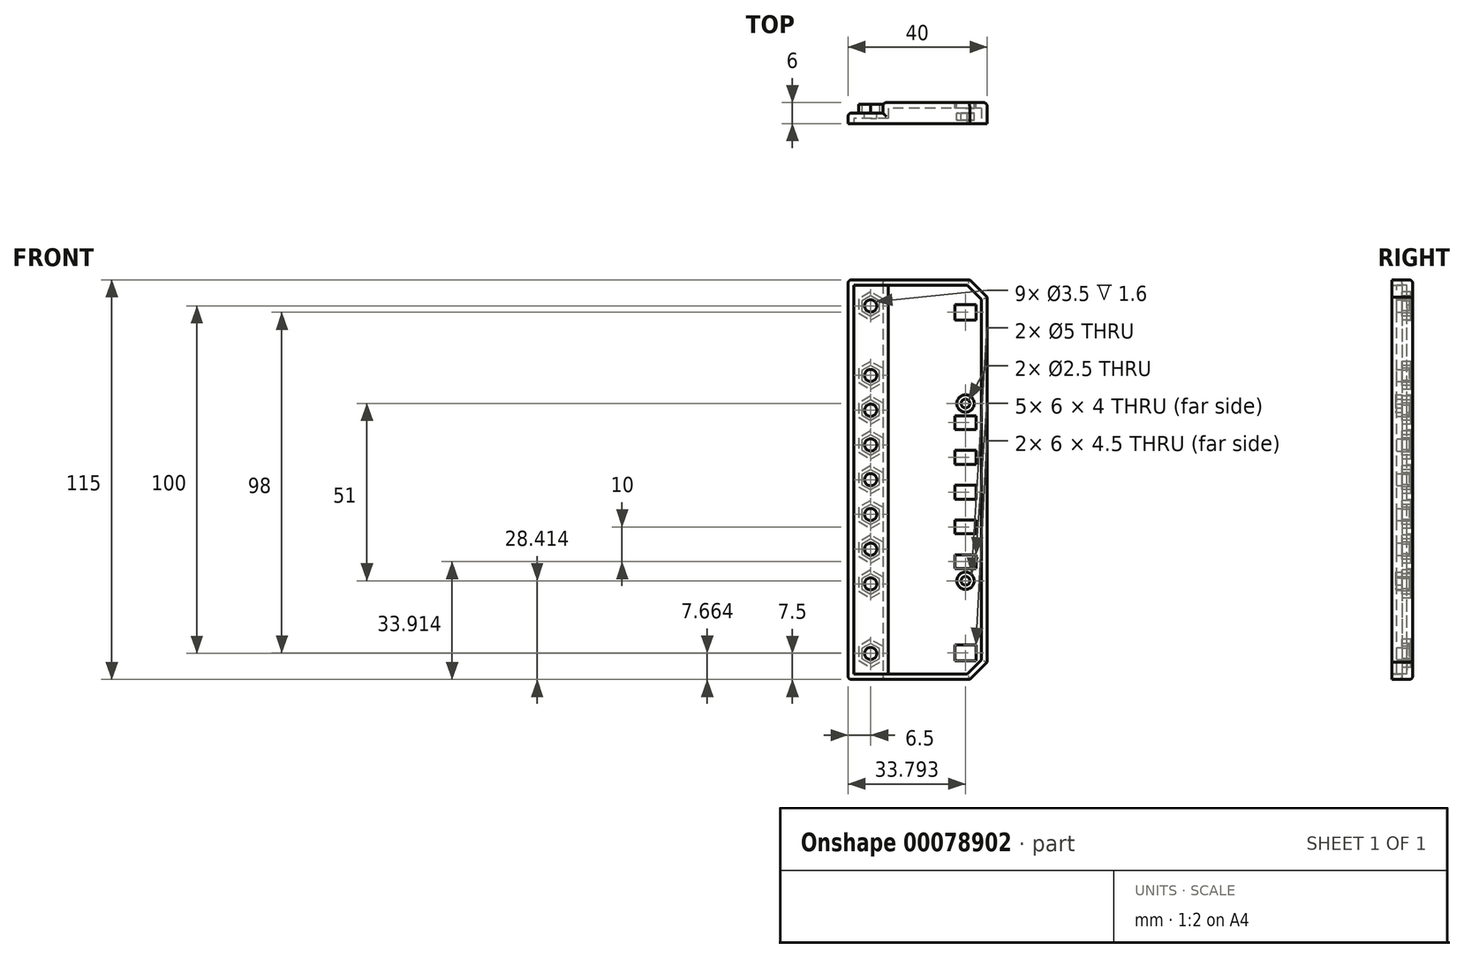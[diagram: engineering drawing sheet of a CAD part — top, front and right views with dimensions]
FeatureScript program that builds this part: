
annotation { "Feature Type Name" : "Feature", "Feature Type Description" : "" }
export const myFeature = defineFeature(function(context is Context, id is Id, definition is map)
    precondition{}
    {
        {
            var Q0;
            Q0=qCreatedBy(makeId("Top.planeOp"),FACE);
            var sketch = newSketch(context, id + "F0", { "sketchPlane" : qUnion([Q0])});
            skLineSegment(sketch, "E0", {"start": v(-20, 3) * mm, "end": v(-20, 0) * mm});
            skLineSegment(sketch, "E1", {"start": v(-20, 0) * mm, "end": v(20, 0) * mm});
            skLineSegment(sketch, "E2", {"start": v(20, 0) * mm, "end": v(20, 6) * mm});
            skLineSegment(sketch, "E3", {"start": v(20, 6) * mm, "end": v(-10, 6) * mm});
            skLineSegment(sketch, "E4", {"start": v(-10, 6) * mm, "end": v(-10, 3) * mm});
            skLineSegment(sketch, "E5", {"start": v(-10, 3) * mm, "end": v(-20, 3) * mm});
            skSolve(sketch);
        }
        {
            var Q0;
            Q0 = qSketchRegion(id + "F0", true);
            extrude(context, id + "F1", {"entities" : qUnion([Q0]), "depth" : 115 * mm});
        }
        {
            var Q0;
            Q0=makeQuery(id+"F1.opExtrude","CAP_EDGE",EDGE,{"disambiguationData":[OSD([sQuery(id+"F0.wireOp",EDGE,"E2")])],"isStart":false});
            var Q1;
            Q1=makeQuery(id+"F1.opExtrude","CAP_EDGE",EDGE,{"disambiguationData":[OSD([sQuery(id+"F0.wireOp",EDGE,"E2")])],"isStart":true});
            chamfer(context, id + "F2", {"entities" : qUnion([Q0, Q1]), "width" : 5 * mm, "tangentPropagation" : true});
        }
        {
            var Q0;
            Q0=makeQuery(id+"F1.opExtrude","CAP_EDGE",EDGE,{"disambiguationData":[OSD([sQuery(id+"F0.wireOp",EDGE,"E0")])],"isStart":true});
            var Q1;
            Q1=makeQuery(id+"F1.opExtrude","CAP_EDGE",EDGE,{"disambiguationData":[OSD([sQuery(id+"F0.wireOp",EDGE,"E4")])],"isStart":true});
            var Q2;
            Q2=makeQuery(id+"F1.opExtrude","CAP_EDGE",EDGE,{"disambiguationData":[OSD([sQuery(id+"F0.wireOp",EDGE,"E4")])],"isStart":false});
            var Q3;
            Q3=makeQuery(id+"F1.opExtrude","CAP_EDGE",EDGE,{"disambiguationData":[OSD([sQuery(id+"F0.wireOp",EDGE,"E0")])],"isStart":false});
            var Q4;
            Q4=makeQuery(id+"F1.opExtrude","SWEPT_EDGE",EDGE,{"disambiguationData":[OSD([sQuery(id+"F0.wireOp",EDGE,"E3"),sQuery(id+"F0.wireOp",EDGE,"E4")])]});
            var Q5;
            Q5=makeQuery(id+"F1.opExtrude","SWEPT_EDGE",EDGE,{"disambiguationData":[OSD([sQuery(id+"F0.wireOp",EDGE,"E0"),sQuery(id+"F0.wireOp",EDGE,"E5")])]});
            var Q6;
            Q6=makeQuery(id+"F1.opExtrude","CAP_EDGE",EDGE,{"disambiguationData":[OSD([sQuery(id+"F0.wireOp",EDGE,"E5")])],"isStart":true});
            var Q7;
            Q7=makeQuery(id+"F1.opExtrude","CAP_EDGE",EDGE,{"disambiguationData":[OSD([sQuery(id+"F0.wireOp",EDGE,"E5")])],"isStart":false});
            var Q8;
            Q8=makeQuery(id+"F1.opExtrude","CAP_EDGE",EDGE,{"disambiguationData":[OSD([sQuery(id+"F0.wireOp",EDGE,"E3")])],"isStart":false});
            var Q9;
            Q9=makeQuery(id+"F1.opExtrude","SWEPT_EDGE",EDGE,{"disambiguationData":[OSD([sQuery(id+"F0.wireOp",EDGE,"E2"),sQuery(id+"F0.wireOp",EDGE,"E3")])]});
            var Q10;
            Q10=makeQuery(id+"F1.opExtrude","CAP_EDGE",EDGE,{"disambiguationData":[OSD([sQuery(id+"F0.wireOp",EDGE,"E3")])],"isStart":true});
            var Q11;
            Q11=makeQuery(id+"F2.opChamfer","BLEND_EDGE",EDGE,{"blendedFrom":[makeQuery(id+"F1.opExtrude","CAP_EDGE",EDGE,{"disambiguationData":[OSD([sQuery(id+"F0.wireOp",EDGE,"E2")])],"isStart":false}),makeQuery(id+"F1.opExtrude","SWEPT_FACE",FACE,{"disambiguationData":[OSD([sQuery(id+"F0.wireOp",EDGE,"E3")])]})],"blendedInto":[makeQuery(id+"F1.opExtrude","SWEPT_FACE",FACE,{"disambiguationData":[OSD([sQuery(id+"F0.wireOp",EDGE,"E3")])]})]});
            var Q12;
            Q12=makeQuery(id+"F2.opChamfer","BLEND_EDGE",EDGE,{"blendedFrom":[makeQuery(id+"F1.opExtrude","CAP_EDGE",EDGE,{"disambiguationData":[OSD([sQuery(id+"F0.wireOp",EDGE,"E2")])],"isStart":true}),makeQuery(id+"F1.opExtrude","SWEPT_FACE",FACE,{"disambiguationData":[OSD([sQuery(id+"F0.wireOp",EDGE,"E3")])]})],"blendedInto":[makeQuery(id+"F1.opExtrude","SWEPT_FACE",FACE,{"disambiguationData":[OSD([sQuery(id+"F0.wireOp",EDGE,"E3")])]})]});
            fillet(context, id + "F3", {"entities" : qUnion([Q0, Q1, Q2, Q3, Q4, Q5, Q6, Q7, Q8, Q9, Q10, Q11, Q12]), "radius" : 1 * mm, "tangentPropagation" : true, "allowEdgeOverflow" : false});
        }
        {
            var Q0;
            Q0=makeQuery(id+"F1.opExtrude","SWEPT_FACE",FACE,{"disambiguationData":[OSD([sQuery(id+"F0.wireOp",EDGE,"E1")])]});
            shell(context, id + "F4", {"entities" : qUnion([Q0]), "thickness" : 1.6 * mm});
        }
        {
            var Q0;
            Q0=makeQuery(id+"F1.opExtrude","SWEPT_FACE",FACE,{"disambiguationData":[OSD([sQuery(id+"F0.wireOp",EDGE,"E3")])]});
            var sketch = newSketch(context, id + "F5", { "sketchPlane" : qUnion([Q0])});
            skLineSegment(sketch, "E6.0", {"start": v(-20, 5) * mm, "end": v(-20, 110) * mm});
            skLineSegment(sketch, "E7.bottom", {"start": v(-10.8, 75.91) * mm, "end": v(-16.8, 75.91) * mm});
            skLineSegment(sketch, "E7.top", {"start": v(-10.8, 71.91) * mm, "end": v(-16.8, 71.91) * mm});
            skLineSegment(sketch, "E7.left", {"start": v(-10.8, 75.91) * mm, "end": v(-10.8, 71.91) * mm});
            skLineSegment(sketch, "E7.right", {"start": v(-16.8, 75.91) * mm, "end": v(-16.8, 71.91) * mm});
            skLineSegment(sketch, "E8.0.1.0", {"start": v(-10.8, 65.91) * mm, "end": v(-16.8, 65.91) * mm});
            skLineSegment(sketch, "E8.0.1.1", {"start": v(-10.8, 61.91) * mm, "end": v(-16.8, 61.91) * mm});
            skLineSegment(sketch, "E8.0.1.2", {"start": v(-10.8, 65.91) * mm, "end": v(-10.8, 61.91) * mm});
            skLineSegment(sketch, "E8.0.1.3", {"start": v(-16.8, 65.91) * mm, "end": v(-16.8, 61.91) * mm});
            skLineSegment(sketch, "E8.0.2.0", {"start": v(-10.8, 55.91) * mm, "end": v(-16.8, 55.91) * mm});
            skLineSegment(sketch, "E8.0.2.1", {"start": v(-10.8, 51.91) * mm, "end": v(-16.8, 51.91) * mm});
            skLineSegment(sketch, "E8.0.2.2", {"start": v(-10.8, 55.91) * mm, "end": v(-10.8, 51.91) * mm});
            skLineSegment(sketch, "E8.0.2.3", {"start": v(-16.8, 55.91) * mm, "end": v(-16.8, 51.91) * mm});
            skLineSegment(sketch, "E8.0.3.0", {"start": v(-10.8, 45.91) * mm, "end": v(-16.8, 45.91) * mm});
            skLineSegment(sketch, "E8.0.3.1", {"start": v(-10.8, 41.91) * mm, "end": v(-16.8, 41.91) * mm});
            skLineSegment(sketch, "E8.0.3.2", {"start": v(-10.8, 45.91) * mm, "end": v(-10.8, 41.91) * mm});
            skLineSegment(sketch, "E8.0.3.3", {"start": v(-16.8, 45.91) * mm, "end": v(-16.8, 41.91) * mm});
            skLineSegment(sketch, "E8.0.4.0", {"start": v(-10.8, 35.91) * mm, "end": v(-16.8, 35.91) * mm});
            skLineSegment(sketch, "E8.0.4.1", {"start": v(-10.8, 31.91) * mm, "end": v(-16.8, 31.91) * mm});
            skLineSegment(sketch, "E8.0.4.2", {"start": v(-10.8, 35.91) * mm, "end": v(-10.8, 31.91) * mm});
            skLineSegment(sketch, "E8.0.4.3", {"start": v(-16.8, 35.91) * mm, "end": v(-16.8, 31.91) * mm});
            skLineSegment(sketch, "E8.direction1", {"start": v(-16.8, 71.91) * mm, "end": v(-17, 71.91) * mm, "construction": true});
            skLineSegment(sketch, "E8.direction2", {"start": v(-16.8, 71.91) * mm, "end": v(-16.8, 61.91) * mm, "construction": true});
            skCircle(sketch, "E9", {"center": v(-13.8, 79.41) * mm, "radius": 2.5 * mm});
            skPoint(sketch, "E9.centerSnap0", {"position": v(-13.8, 75.91) * mm});
            skCircle(sketch, "E10", {"center": v(-13.8, 28.41) * mm, "radius": 2.5 * mm});
            skPoint(sketch, "E10.centerSnap0", {"position": v(-13.8, 31.91) * mm});
            skCircle(sketch, "E11", {"center": v(-13.8, 28.41) * mm, "radius": 1.25 * mm});
            skCircle(sketch, "E12", {"center": v(-13.8, 79.41) * mm, "radius": 1.25 * mm});
            skLineSegment(sketch, "E13.bottom", {"start": v(-10.8, 103.41) * mm, "end": v(-16.8, 103.41) * mm});
            skLineSegment(sketch, "E13.top", {"start": v(-10.8, 107.91) * mm, "end": v(-16.8, 107.91) * mm});
            skLineSegment(sketch, "E13.left", {"start": v(-10.8, 103.41) * mm, "end": v(-10.8, 107.91) * mm});
            skLineSegment(sketch, "E13.right", {"start": v(-16.8, 103.41) * mm, "end": v(-16.8, 107.91) * mm});
            skPoint(sketch, "E13.middle", {"position": v(-13.8, 105.66) * mm});
            skLineSegment(sketch, "E14.bottom", {"start": v(-16.8, 5.41) * mm, "end": v(-10.8, 5.41) * mm});
            skLineSegment(sketch, "E14.top", {"start": v(-16.8, 9.91) * mm, "end": v(-10.8, 9.91) * mm});
            skLineSegment(sketch, "E14.left", {"start": v(-16.8, 5.41) * mm, "end": v(-16.8, 9.91) * mm});
            skLineSegment(sketch, "E14.right", {"start": v(-10.8, 5.41) * mm, "end": v(-10.8, 9.91) * mm});
            skPoint(sketch, "E14.middle", {"position": v(-13.8, 7.66) * mm});
            skPoint(sketch, "E14.cornerSnap0", {"position": v(-16.8, 3.2) * mm});
            skSolve(sketch);
        }
        {
            var Q0;
            Q0=makeQuery(id+"F5.imprint","IMPRINT",FACE,{"disambiguationData":[TD([[makeQuery(id+"F5.imprint","IMPRINT",EDGE,{"derivedFrom":sQuery(id+"F5.wireOp",EDGE,"E7.bottom")}),1.0]])]});
            var Q1;
            Q1=makeQuery(id+"F5.imprint","IMPRINT",FACE,{"disambiguationData":[TD([[makeQuery(id+"F5.imprint","IMPRINT",EDGE,{"derivedFrom":sQuery(id+"F5.wireOp",EDGE,"E8.0.1.0")}),1.0]])]});
            var Q2;
            Q2=makeQuery(id+"F5.imprint","IMPRINT",FACE,{"disambiguationData":[TD([[makeQuery(id+"F5.imprint","IMPRINT",EDGE,{"derivedFrom":sQuery(id+"F5.wireOp",EDGE,"E8.0.2.0")}),1.0]])]});
            var Q3;
            Q3=makeQuery(id+"F5.imprint","IMPRINT",FACE,{"disambiguationData":[TD([[makeQuery(id+"F5.imprint","IMPRINT",EDGE,{"derivedFrom":sQuery(id+"F5.wireOp",EDGE,"E8.0.3.0")}),1.0]])]});
            var Q4;
            Q4=makeQuery(id+"F5.imprint","IMPRINT",FACE,{"disambiguationData":[TD([[makeQuery(id+"F5.imprint","IMPRINT",EDGE,{"derivedFrom":sQuery(id+"F5.wireOp",EDGE,"E8.0.4.0")}),1.0]])]});
            var Q5;
            Q5=makeQuery(id+"F5.imprint","IMPRINT",FACE,{"disambiguationData":[TD([[makeQuery(id+"F5.imprint","IMPRINT",EDGE,{"derivedFrom":sQuery(id+"F5.wireOp",EDGE,"E13.bottom")}),-1.0]])]});
            var Q6;
            Q6=makeQuery(id+"F5.imprint","IMPRINT",FACE,{"disambiguationData":[TD([[makeQuery(id+"F5.imprint","IMPRINT",EDGE,{"derivedFrom":sQuery(id+"F5.wireOp",EDGE,"E14.bottom")}),1.0]])]});
            var Q7;
            Q7=makeQuery(id+"F5.imprint","IMPRINT",FACE,{"disambiguationData":[TD([[makeQuery(id+"F5.imprint","IMPRINT",EDGE,{"derivedFrom":sQuery(id+"F5.wireOp",EDGE,"E12")}),1.0]])]});
            var Q8;
            Q8=makeQuery(id+"F5.imprint","IMPRINT",FACE,{"disambiguationData":[TD([[makeQuery(id+"F5.imprint","IMPRINT",EDGE,{"derivedFrom":sQuery(id+"F5.wireOp",EDGE,"E11")}),1.0]])]});
            extrude(context, id + "F6", {"entities" : qUnion([Q0, Q1, Q2, Q3, Q4, Q5, Q6, Q7, Q8]), "operationType" : NewBodyOperationType.REMOVE, "oppositeDirection" : true, "depth" : 100 * mm});
        }
        {
            var Q0;
            Q0=makeQuery(id+"F5.imprint","IMPRINT",FACE,{"disambiguationData":[TD([[makeQuery(id+"F5.imprint","IMPRINT",EDGE,{"derivedFrom":sQuery(id+"F5.wireOp",EDGE,"E9")}),1.0]])]});
            var Q1;
            Q1=makeQuery(id+"F5.imprint","IMPRINT",FACE,{"disambiguationData":[TD([[makeQuery(id+"F5.imprint","IMPRINT",EDGE,{"derivedFrom":sQuery(id+"F5.wireOp",EDGE,"E10")}),1.0]])]});
            extrude(context, id + "F7", {"entities" : qUnion([Q0, Q1]), "operationType" : NewBodyOperationType.ADD, "oppositeDirection" : true, "depth" : 5 * mm});
        }
        {
            var Q0;
            Q0=makeQuery(id+"F1.opExtrude","SWEPT_FACE",FACE,{"disambiguationData":[OSD([sQuery(id+"F0.wireOp",EDGE,"E5")])]});
            var sketch = newSketch(context, id + "F8", { "sketchPlane" : qUnion([Q0])});
            skCircle(sketch, "E15", {"center": v(13.5, 107.5) * mm, "radius": 1.75 * mm});
            skLineSegment(sketch, "E16.0.3", {"start": v(20, 1) * mm, "end": v(20, 114) * mm});
            skCircle(sketch, "E17.0.1.0", {"center": v(13.5, 97.5) * mm, "radius": 1.75 * mm});
            skCircle(sketch, "E17.0.2.0", {"center": v(13.5, 87.5) * mm, "radius": 1.75 * mm});
            skCircle(sketch, "E17.0.3.0", {"center": v(13.5, 77.5) * mm, "radius": 1.75 * mm});
            skCircle(sketch, "E17.0.4.0", {"center": v(13.5, 67.5) * mm, "radius": 1.75 * mm});
            skCircle(sketch, "E17.0.5.0", {"center": v(13.5, 57.5) * mm, "radius": 1.75 * mm});
            skCircle(sketch, "E17.0.6.0", {"center": v(13.5, 47.5) * mm, "radius": 1.75 * mm});
            skCircle(sketch, "E17.0.7.0", {"center": v(13.5, 37.5) * mm, "radius": 1.75 * mm});
            skCircle(sketch, "E17.0.8.0", {"center": v(13.5, 27.5) * mm, "radius": 1.75 * mm});
            skCircle(sketch, "E17.0.9.0", {"center": v(13.5, 17.5) * mm, "radius": 1.75 * mm});
            skCircle(sketch, "E17.0.10.0", {"center": v(13.5, 7.5) * mm, "radius": 1.75 * mm});
            skLineSegment(sketch, "E17.direction1", {"start": v(13.5, 107.5) * mm, "end": v(16.25, 107.5) * mm, "construction": true});
            skLineSegment(sketch, "E17.direction2", {"start": v(13.5, 107.5) * mm, "end": v(13.5, 97.5) * mm, "construction": true});
            skPoint(sketch, "E18", {"position": v(20, 57.5) * mm});
            skCircle(sketch, "E19.cCircle", {"center": v(13.5, 7.5) * mm, "radius": 3.5 * mm, "construction": true});
            skLineSegment(sketch, "E19.0", {"start": v(10, 9.52) * mm, "end": v(13.5, 11.54) * mm});
            skLineSegment(sketch, "E19.1", {"start": v(13.5, 11.54) * mm, "end": v(17, 9.52) * mm});
            skLineSegment(sketch, "E19.2", {"start": v(17, 9.52) * mm, "end": v(17, 5.48) * mm});
            skLineSegment(sketch, "E19.3", {"start": v(17, 5.48) * mm, "end": v(13.5, 3.46) * mm});
            skLineSegment(sketch, "E19.4", {"start": v(13.5, 3.46) * mm, "end": v(10, 5.48) * mm});
            skLineSegment(sketch, "E19.5", {"start": v(10, 5.48) * mm, "end": v(10, 9.52) * mm});
            skPoint(sketch, "E19.0.midPoint", {"position": v(11.75, 10.53) * mm});
            skLineSegment(sketch, "E20.0", {"start": v(16, 6.06) * mm, "end": v(13.5, 4.61) * mm});
            skLineSegment(sketch, "E20.1", {"start": v(11, 6.06) * mm, "end": v(11, 8.94) * mm});
            skLineSegment(sketch, "E20.2", {"start": v(11, 8.94) * mm, "end": v(13.5, 10.39) * mm});
            skLineSegment(sketch, "E20.3", {"start": v(13.5, 4.61) * mm, "end": v(11, 6.06) * mm});
            skLineSegment(sketch, "E20.4", {"start": v(13.5, 10.39) * mm, "end": v(16, 8.94) * mm});
            skLineSegment(sketch, "E20.5", {"start": v(16, 8.94) * mm, "end": v(16, 6.06) * mm});
            skPoint(sketch, "E21.0.1.0", {"position": v(11.75, 20.53) * mm});
            skLineSegment(sketch, "E21.0.1.1", {"start": v(10, 15.48) * mm, "end": v(10, 19.52) * mm});
            skCircle(sketch, "E21.0.1.2", {"center": v(13.5, 17.5) * mm, "radius": 3.5 * mm, "construction": true});
            skLineSegment(sketch, "E21.0.1.3", {"start": v(11, 16.06) * mm, "end": v(11, 18.94) * mm});
            skLineSegment(sketch, "E21.0.1.4", {"start": v(13.5, 20.39) * mm, "end": v(16, 18.94) * mm});
            skLineSegment(sketch, "E21.0.1.5", {"start": v(16, 18.94) * mm, "end": v(16, 16.06) * mm});
            skLineSegment(sketch, "E21.0.1.6", {"start": v(16, 16.06) * mm, "end": v(13.5, 14.61) * mm});
            skLineSegment(sketch, "E21.0.1.7", {"start": v(17, 15.48) * mm, "end": v(13.5, 13.46) * mm});
            skLineSegment(sketch, "E21.0.1.8", {"start": v(13.5, 21.54) * mm, "end": v(17, 19.52) * mm});
            skLineSegment(sketch, "E21.0.1.9", {"start": v(17, 19.52) * mm, "end": v(17, 15.48) * mm});
            skLineSegment(sketch, "E21.0.1.10", {"start": v(10, 19.52) * mm, "end": v(13.5, 21.54) * mm});
            skLineSegment(sketch, "E21.0.1.11", {"start": v(13.5, 13.46) * mm, "end": v(10, 15.48) * mm});
            skLineSegment(sketch, "E21.0.1.12", {"start": v(11, 18.94) * mm, "end": v(13.5, 20.39) * mm});
            skLineSegment(sketch, "E21.0.1.13", {"start": v(13.5, 14.61) * mm, "end": v(11, 16.06) * mm});
            skPoint(sketch, "E21.0.2.0", {"position": v(11.75, 30.53) * mm});
            skLineSegment(sketch, "E21.0.2.1", {"start": v(10, 25.48) * mm, "end": v(10, 29.52) * mm});
            skCircle(sketch, "E21.0.2.2", {"center": v(13.5, 27.5) * mm, "radius": 3.5 * mm, "construction": true});
            skLineSegment(sketch, "E21.0.2.3", {"start": v(11, 26.06) * mm, "end": v(11, 28.94) * mm});
            skLineSegment(sketch, "E21.0.2.4", {"start": v(13.5, 30.39) * mm, "end": v(16, 28.94) * mm});
            skLineSegment(sketch, "E21.0.2.5", {"start": v(16, 28.94) * mm, "end": v(16, 26.06) * mm});
            skLineSegment(sketch, "E21.0.2.6", {"start": v(16, 26.06) * mm, "end": v(13.5, 24.61) * mm});
            skLineSegment(sketch, "E21.0.2.7", {"start": v(17, 25.48) * mm, "end": v(13.5, 23.46) * mm});
            skLineSegment(sketch, "E21.0.2.8", {"start": v(13.5, 31.54) * mm, "end": v(17, 29.52) * mm});
            skLineSegment(sketch, "E21.0.2.9", {"start": v(17, 29.52) * mm, "end": v(17, 25.48) * mm});
            skLineSegment(sketch, "E21.0.2.10", {"start": v(10, 29.52) * mm, "end": v(13.5, 31.54) * mm});
            skLineSegment(sketch, "E21.0.2.11", {"start": v(13.5, 23.46) * mm, "end": v(10, 25.48) * mm});
            skLineSegment(sketch, "E21.0.2.12", {"start": v(11, 28.94) * mm, "end": v(13.5, 30.39) * mm});
            skLineSegment(sketch, "E21.0.2.13", {"start": v(13.5, 24.61) * mm, "end": v(11, 26.06) * mm});
            skPoint(sketch, "E21.0.3.0", {"position": v(11.75, 40.53) * mm});
            skLineSegment(sketch, "E21.0.3.1", {"start": v(10, 35.48) * mm, "end": v(10, 39.52) * mm});
            skCircle(sketch, "E21.0.3.2", {"center": v(13.5, 37.5) * mm, "radius": 3.5 * mm, "construction": true});
            skLineSegment(sketch, "E21.0.3.3", {"start": v(11, 36.06) * mm, "end": v(11, 38.94) * mm});
            skLineSegment(sketch, "E21.0.3.4", {"start": v(13.5, 40.39) * mm, "end": v(16, 38.94) * mm});
            skLineSegment(sketch, "E21.0.3.5", {"start": v(16, 38.94) * mm, "end": v(16, 36.06) * mm});
            skLineSegment(sketch, "E21.0.3.6", {"start": v(16, 36.06) * mm, "end": v(13.5, 34.61) * mm});
            skLineSegment(sketch, "E21.0.3.7", {"start": v(17, 35.48) * mm, "end": v(13.5, 33.46) * mm});
            skLineSegment(sketch, "E21.0.3.8", {"start": v(13.5, 41.54) * mm, "end": v(17, 39.52) * mm});
            skLineSegment(sketch, "E21.0.3.9", {"start": v(17, 39.52) * mm, "end": v(17, 35.48) * mm});
            skLineSegment(sketch, "E21.0.3.10", {"start": v(10, 39.52) * mm, "end": v(13.5, 41.54) * mm});
            skLineSegment(sketch, "E21.0.3.11", {"start": v(13.5, 33.46) * mm, "end": v(10, 35.48) * mm});
            skLineSegment(sketch, "E21.0.3.12", {"start": v(11, 38.94) * mm, "end": v(13.5, 40.39) * mm});
            skLineSegment(sketch, "E21.0.3.13", {"start": v(13.5, 34.61) * mm, "end": v(11, 36.06) * mm});
            skPoint(sketch, "E21.0.4.0", {"position": v(11.75, 50.53) * mm});
            skLineSegment(sketch, "E21.0.4.1", {"start": v(10, 45.48) * mm, "end": v(10, 49.52) * mm});
            skCircle(sketch, "E21.0.4.2", {"center": v(13.5, 47.5) * mm, "radius": 3.5 * mm, "construction": true});
            skLineSegment(sketch, "E21.0.4.3", {"start": v(11, 46.06) * mm, "end": v(11, 48.94) * mm});
            skLineSegment(sketch, "E21.0.4.4", {"start": v(13.5, 50.39) * mm, "end": v(16, 48.94) * mm});
            skLineSegment(sketch, "E21.0.4.5", {"start": v(16, 48.94) * mm, "end": v(16, 46.06) * mm});
            skLineSegment(sketch, "E21.0.4.6", {"start": v(16, 46.06) * mm, "end": v(13.5, 44.61) * mm});
            skLineSegment(sketch, "E21.0.4.7", {"start": v(17, 45.48) * mm, "end": v(13.5, 43.46) * mm});
            skLineSegment(sketch, "E21.0.4.8", {"start": v(13.5, 51.54) * mm, "end": v(17, 49.52) * mm});
            skLineSegment(sketch, "E21.0.4.9", {"start": v(17, 49.52) * mm, "end": v(17, 45.48) * mm});
            skLineSegment(sketch, "E21.0.4.10", {"start": v(10, 49.52) * mm, "end": v(13.5, 51.54) * mm});
            skLineSegment(sketch, "E21.0.4.11", {"start": v(13.5, 43.46) * mm, "end": v(10, 45.48) * mm});
            skLineSegment(sketch, "E21.0.4.12", {"start": v(11, 48.94) * mm, "end": v(13.5, 50.39) * mm});
            skLineSegment(sketch, "E21.0.4.13", {"start": v(13.5, 44.61) * mm, "end": v(11, 46.06) * mm});
            skPoint(sketch, "E21.0.5.0", {"position": v(11.75, 60.53) * mm});
            skLineSegment(sketch, "E21.0.5.1", {"start": v(10, 55.48) * mm, "end": v(10, 59.52) * mm});
            skCircle(sketch, "E21.0.5.2", {"center": v(13.5, 57.5) * mm, "radius": 3.5 * mm, "construction": true});
            skLineSegment(sketch, "E21.0.5.3", {"start": v(11, 56.06) * mm, "end": v(11, 58.94) * mm});
            skLineSegment(sketch, "E21.0.5.4", {"start": v(13.5, 60.39) * mm, "end": v(16, 58.94) * mm});
            skLineSegment(sketch, "E21.0.5.5", {"start": v(16, 58.94) * mm, "end": v(16, 56.06) * mm});
            skLineSegment(sketch, "E21.0.5.6", {"start": v(16, 56.06) * mm, "end": v(13.5, 54.61) * mm});
            skLineSegment(sketch, "E21.0.5.7", {"start": v(17, 55.48) * mm, "end": v(13.5, 53.46) * mm});
            skLineSegment(sketch, "E21.0.5.8", {"start": v(13.5, 61.54) * mm, "end": v(17, 59.52) * mm});
            skLineSegment(sketch, "E21.0.5.9", {"start": v(17, 59.52) * mm, "end": v(17, 55.48) * mm});
            skLineSegment(sketch, "E21.0.5.10", {"start": v(10, 59.52) * mm, "end": v(13.5, 61.54) * mm});
            skLineSegment(sketch, "E21.0.5.11", {"start": v(13.5, 53.46) * mm, "end": v(10, 55.48) * mm});
            skLineSegment(sketch, "E21.0.5.12", {"start": v(11, 58.94) * mm, "end": v(13.5, 60.39) * mm});
            skLineSegment(sketch, "E21.0.5.13", {"start": v(13.5, 54.61) * mm, "end": v(11, 56.06) * mm});
            skPoint(sketch, "E21.0.6.0", {"position": v(11.75, 70.53) * mm});
            skLineSegment(sketch, "E21.0.6.1", {"start": v(10, 65.48) * mm, "end": v(10, 69.52) * mm});
            skCircle(sketch, "E21.0.6.2", {"center": v(13.5, 67.5) * mm, "radius": 3.5 * mm, "construction": true});
            skLineSegment(sketch, "E21.0.6.3", {"start": v(11, 66.06) * mm, "end": v(11, 68.94) * mm});
            skLineSegment(sketch, "E21.0.6.4", {"start": v(13.5, 70.39) * mm, "end": v(16, 68.94) * mm});
            skLineSegment(sketch, "E21.0.6.5", {"start": v(16, 68.94) * mm, "end": v(16, 66.06) * mm});
            skLineSegment(sketch, "E21.0.6.6", {"start": v(16, 66.06) * mm, "end": v(13.5, 64.61) * mm});
            skLineSegment(sketch, "E21.0.6.7", {"start": v(17, 65.48) * mm, "end": v(13.5, 63.46) * mm});
            skLineSegment(sketch, "E21.0.6.8", {"start": v(13.5, 71.54) * mm, "end": v(17, 69.52) * mm});
            skLineSegment(sketch, "E21.0.6.9", {"start": v(17, 69.52) * mm, "end": v(17, 65.48) * mm});
            skLineSegment(sketch, "E21.0.6.10", {"start": v(10, 69.52) * mm, "end": v(13.5, 71.54) * mm});
            skLineSegment(sketch, "E21.0.6.11", {"start": v(13.5, 63.46) * mm, "end": v(10, 65.48) * mm});
            skLineSegment(sketch, "E21.0.6.12", {"start": v(11, 68.94) * mm, "end": v(13.5, 70.39) * mm});
            skLineSegment(sketch, "E21.0.6.13", {"start": v(13.5, 64.61) * mm, "end": v(11, 66.06) * mm});
            skPoint(sketch, "E21.0.7.0", {"position": v(11.75, 80.53) * mm});
            skLineSegment(sketch, "E21.0.7.1", {"start": v(10, 75.48) * mm, "end": v(10, 79.52) * mm});
            skCircle(sketch, "E21.0.7.2", {"center": v(13.5, 77.5) * mm, "radius": 3.5 * mm, "construction": true});
            skLineSegment(sketch, "E21.0.7.3", {"start": v(11, 76.06) * mm, "end": v(11, 78.94) * mm});
            skLineSegment(sketch, "E21.0.7.4", {"start": v(13.5, 80.39) * mm, "end": v(16, 78.94) * mm});
            skLineSegment(sketch, "E21.0.7.5", {"start": v(16, 78.94) * mm, "end": v(16, 76.06) * mm});
            skLineSegment(sketch, "E21.0.7.6", {"start": v(16, 76.06) * mm, "end": v(13.5, 74.61) * mm});
            skLineSegment(sketch, "E21.0.7.7", {"start": v(17, 75.48) * mm, "end": v(13.5, 73.46) * mm});
            skLineSegment(sketch, "E21.0.7.8", {"start": v(13.5, 81.54) * mm, "end": v(17, 79.52) * mm});
            skLineSegment(sketch, "E21.0.7.9", {"start": v(17, 79.52) * mm, "end": v(17, 75.48) * mm});
            skLineSegment(sketch, "E21.0.7.10", {"start": v(10, 79.52) * mm, "end": v(13.5, 81.54) * mm});
            skLineSegment(sketch, "E21.0.7.11", {"start": v(13.5, 73.46) * mm, "end": v(10, 75.48) * mm});
            skLineSegment(sketch, "E21.0.7.12", {"start": v(11, 78.94) * mm, "end": v(13.5, 80.39) * mm});
            skLineSegment(sketch, "E21.0.7.13", {"start": v(13.5, 74.61) * mm, "end": v(11, 76.06) * mm});
            skPoint(sketch, "E21.0.8.0", {"position": v(11.75, 90.53) * mm});
            skLineSegment(sketch, "E21.0.8.1", {"start": v(10, 85.48) * mm, "end": v(10, 89.52) * mm});
            skCircle(sketch, "E21.0.8.2", {"center": v(13.5, 87.5) * mm, "radius": 3.5 * mm, "construction": true});
            skLineSegment(sketch, "E21.0.8.3", {"start": v(11, 86.06) * mm, "end": v(11, 88.94) * mm});
            skLineSegment(sketch, "E21.0.8.4", {"start": v(13.5, 90.39) * mm, "end": v(16, 88.94) * mm});
            skLineSegment(sketch, "E21.0.8.5", {"start": v(16, 88.94) * mm, "end": v(16, 86.06) * mm});
            skLineSegment(sketch, "E21.0.8.6", {"start": v(16, 86.06) * mm, "end": v(13.5, 84.61) * mm});
            skLineSegment(sketch, "E21.0.8.7", {"start": v(17, 85.48) * mm, "end": v(13.5, 83.46) * mm});
            skLineSegment(sketch, "E21.0.8.8", {"start": v(13.5, 91.54) * mm, "end": v(17, 89.52) * mm});
            skLineSegment(sketch, "E21.0.8.9", {"start": v(17, 89.52) * mm, "end": v(17, 85.48) * mm});
            skLineSegment(sketch, "E21.0.8.10", {"start": v(10, 89.52) * mm, "end": v(13.5, 91.54) * mm});
            skLineSegment(sketch, "E21.0.8.11", {"start": v(13.5, 83.46) * mm, "end": v(10, 85.48) * mm});
            skLineSegment(sketch, "E21.0.8.12", {"start": v(11, 88.94) * mm, "end": v(13.5, 90.39) * mm});
            skLineSegment(sketch, "E21.0.8.13", {"start": v(13.5, 84.61) * mm, "end": v(11, 86.06) * mm});
            skPoint(sketch, "E21.0.9.0", {"position": v(11.75, 100.53) * mm});
            skLineSegment(sketch, "E21.0.9.1", {"start": v(10, 95.48) * mm, "end": v(10, 99.52) * mm});
            skCircle(sketch, "E21.0.9.2", {"center": v(13.5, 97.5) * mm, "radius": 3.5 * mm, "construction": true});
            skLineSegment(sketch, "E21.0.9.3", {"start": v(11, 96.06) * mm, "end": v(11, 98.94) * mm});
            skLineSegment(sketch, "E21.0.9.4", {"start": v(13.5, 100.39) * mm, "end": v(16, 98.94) * mm});
            skLineSegment(sketch, "E21.0.9.5", {"start": v(16, 98.94) * mm, "end": v(16, 96.06) * mm});
            skLineSegment(sketch, "E21.0.9.6", {"start": v(16, 96.06) * mm, "end": v(13.5, 94.61) * mm});
            skLineSegment(sketch, "E21.0.9.7", {"start": v(17, 95.48) * mm, "end": v(13.5, 93.46) * mm});
            skLineSegment(sketch, "E21.0.9.8", {"start": v(13.5, 101.54) * mm, "end": v(17, 99.52) * mm});
            skLineSegment(sketch, "E21.0.9.9", {"start": v(17, 99.52) * mm, "end": v(17, 95.48) * mm});
            skLineSegment(sketch, "E21.0.9.10", {"start": v(10, 99.52) * mm, "end": v(13.5, 101.54) * mm});
            skLineSegment(sketch, "E21.0.9.11", {"start": v(13.5, 93.46) * mm, "end": v(10, 95.48) * mm});
            skLineSegment(sketch, "E21.0.9.12", {"start": v(11, 98.94) * mm, "end": v(13.5, 100.39) * mm});
            skLineSegment(sketch, "E21.0.9.13", {"start": v(13.5, 94.61) * mm, "end": v(11, 96.06) * mm});
            skPoint(sketch, "E21.0.10.0", {"position": v(11.75, 110.53) * mm});
            skLineSegment(sketch, "E21.0.10.1", {"start": v(10, 105.48) * mm, "end": v(10, 109.52) * mm});
            skCircle(sketch, "E21.0.10.2", {"center": v(13.5, 107.5) * mm, "radius": 3.5 * mm, "construction": true});
            skLineSegment(sketch, "E21.0.10.3", {"start": v(11, 106.06) * mm, "end": v(11, 108.94) * mm});
            skLineSegment(sketch, "E21.0.10.4", {"start": v(13.5, 110.39) * mm, "end": v(16, 108.94) * mm});
            skLineSegment(sketch, "E21.0.10.5", {"start": v(16, 108.94) * mm, "end": v(16, 106.06) * mm});
            skLineSegment(sketch, "E21.0.10.6", {"start": v(16, 106.06) * mm, "end": v(13.5, 104.61) * mm});
            skLineSegment(sketch, "E21.0.10.7", {"start": v(17, 105.48) * mm, "end": v(13.5, 103.46) * mm});
            skLineSegment(sketch, "E21.0.10.8", {"start": v(13.5, 111.54) * mm, "end": v(17, 109.52) * mm});
            skLineSegment(sketch, "E21.0.10.9", {"start": v(17, 109.52) * mm, "end": v(17, 105.48) * mm});
            skLineSegment(sketch, "E21.0.10.10", {"start": v(10, 109.52) * mm, "end": v(13.5, 111.54) * mm});
            skLineSegment(sketch, "E21.0.10.11", {"start": v(13.5, 103.46) * mm, "end": v(10, 105.48) * mm});
            skLineSegment(sketch, "E21.0.10.12", {"start": v(11, 108.94) * mm, "end": v(13.5, 110.39) * mm});
            skLineSegment(sketch, "E21.0.10.13", {"start": v(13.5, 104.61) * mm, "end": v(11, 106.06) * mm});
            skLineSegment(sketch, "E21.direction1", {"start": v(10, 5.48) * mm, "end": v(35, 5.48) * mm, "construction": true});
            skLineSegment(sketch, "E21.direction2", {"start": v(10, 5.48) * mm, "end": v(10, 15.48) * mm, "construction": true});
            skSolve(sketch);
        }
        {
            var Q0;
            Q0=makeQuery(id+"F8.imprint","IMPRINT",FACE,{"disambiguationData":[TD([[makeQuery(id+"F8.imprint","IMPRINT",EDGE,{"derivedFrom":sQuery(id+"F8.wireOp",EDGE,"E17.0.10.0")}),1.0]])]});
            var Q1;
            Q1=makeQuery(id+"F8.imprint","IMPRINT",FACE,{"disambiguationData":[TD([[makeQuery(id+"F8.imprint","IMPRINT",EDGE,{"derivedFrom":sQuery(id+"F8.wireOp",EDGE,"E17.0.8.0")}),1.0]])]});
            var Q2;
            Q2=makeQuery(id+"F8.imprint","IMPRINT",FACE,{"disambiguationData":[TD([[makeQuery(id+"F8.imprint","IMPRINT",EDGE,{"derivedFrom":sQuery(id+"F8.wireOp",EDGE,"E17.0.7.0")}),1.0]])]});
            var Q3;
            Q3=makeQuery(id+"F8.imprint","IMPRINT",FACE,{"disambiguationData":[TD([[makeQuery(id+"F8.imprint","IMPRINT",EDGE,{"derivedFrom":sQuery(id+"F8.wireOp",EDGE,"E17.0.6.0")}),1.0]])]});
            var Q4;
            Q4=makeQuery(id+"F8.imprint","IMPRINT",FACE,{"disambiguationData":[TD([[makeQuery(id+"F8.imprint","IMPRINT",EDGE,{"derivedFrom":sQuery(id+"F8.wireOp",EDGE,"E17.0.5.0")}),1.0]])]});
            var Q5;
            Q5=makeQuery(id+"F8.imprint","IMPRINT",FACE,{"disambiguationData":[TD([[makeQuery(id+"F8.imprint","IMPRINT",EDGE,{"derivedFrom":sQuery(id+"F8.wireOp",EDGE,"E17.0.4.0")}),1.0]])]});
            var Q6;
            Q6=makeQuery(id+"F8.imprint","IMPRINT",FACE,{"disambiguationData":[TD([[makeQuery(id+"F8.imprint","IMPRINT",EDGE,{"derivedFrom":sQuery(id+"F8.wireOp",EDGE,"E17.0.3.0")}),1.0]])]});
            var Q7;
            Q7=makeQuery(id+"F8.imprint","IMPRINT",FACE,{"disambiguationData":[TD([[makeQuery(id+"F8.imprint","IMPRINT",EDGE,{"derivedFrom":sQuery(id+"F8.wireOp",EDGE,"E17.0.2.0")}),1.0]])]});
            var Q8;
            Q8=makeQuery(id+"F8.imprint","IMPRINT",FACE,{"disambiguationData":[TD([[makeQuery(id+"F8.imprint","IMPRINT",EDGE,{"derivedFrom":sQuery(id+"F8.wireOp",EDGE,"E15")}),1.0]])]});
            extrude(context, id + "F9", {"entities" : qUnion([Q0, Q1, Q2, Q3, Q4, Q5, Q6, Q7, Q8]), "operationType" : NewBodyOperationType.REMOVE, "oppositeDirection" : true, "depth" : 25 * mm});
        }
        {
            var Q0;
            Q0=makeQuery(id+"F8.imprint","IMPRINT",FACE,{"disambiguationData":[TD([[makeQuery(id+"F8.imprint","IMPRINT",EDGE,{"derivedFrom":sQuery(id+"F8.wireOp",EDGE,"E19.0")}),-1.0]])]});
            var Q1;
            Q1=makeQuery(id+"F8.imprint","IMPRINT",FACE,{"disambiguationData":[TD([[makeQuery(id+"F8.imprint","IMPRINT",EDGE,{"derivedFrom":sQuery(id+"F8.wireOp",EDGE,"E21.0.2.1")}),1.0]])]});
            var Q2;
            Q2=makeQuery(id+"F8.imprint","IMPRINT",FACE,{"disambiguationData":[TD([[makeQuery(id+"F8.imprint","IMPRINT",EDGE,{"derivedFrom":sQuery(id+"F8.wireOp",EDGE,"E21.0.3.1")}),1.0]])]});
            var Q3;
            Q3=makeQuery(id+"F8.imprint","IMPRINT",FACE,{"disambiguationData":[TD([[makeQuery(id+"F8.imprint","IMPRINT",EDGE,{"derivedFrom":sQuery(id+"F8.wireOp",EDGE,"E21.0.4.1")}),1.0]])]});
            var Q4;
            Q4=makeQuery(id+"F8.imprint","IMPRINT",FACE,{"disambiguationData":[TD([[makeQuery(id+"F8.imprint","IMPRINT",EDGE,{"derivedFrom":sQuery(id+"F8.wireOp",EDGE,"E21.0.5.1")}),1.0]])]});
            var Q5;
            Q5=makeQuery(id+"F8.imprint","IMPRINT",FACE,{"disambiguationData":[TD([[makeQuery(id+"F8.imprint","IMPRINT",EDGE,{"derivedFrom":sQuery(id+"F8.wireOp",EDGE,"E21.0.6.1")}),1.0]])]});
            var Q6;
            Q6=makeQuery(id+"F8.imprint","IMPRINT",FACE,{"disambiguationData":[TD([[makeQuery(id+"F8.imprint","IMPRINT",EDGE,{"derivedFrom":sQuery(id+"F8.wireOp",EDGE,"E21.0.7.1")}),1.0]])]});
            var Q7;
            Q7=makeQuery(id+"F8.imprint","IMPRINT",FACE,{"disambiguationData":[TD([[makeQuery(id+"F8.imprint","IMPRINT",EDGE,{"derivedFrom":sQuery(id+"F8.wireOp",EDGE,"E21.0.8.1")}),1.0]])]});
            var Q8;
            Q8=makeQuery(id+"F8.imprint","IMPRINT",FACE,{"disambiguationData":[TD([[makeQuery(id+"F8.imprint","IMPRINT",EDGE,{"derivedFrom":sQuery(id+"F8.wireOp",EDGE,"E21.0.10.1")}),1.0]])]});
            extrude(context, id + "F10", {"entities" : qUnion([Q0, Q1, Q2, Q3, Q4, Q5, Q6, Q7, Q8]), "operationType" : NewBodyOperationType.ADD, "depth" : 2.5 * mm});
        }
        {
            var Q0;
            Q0=makeQuery(id+"F5.imprint","IMPRINT",FACE,{"disambiguationData":[TD([[makeQuery(id+"F5.imprint","IMPRINT",EDGE,{"derivedFrom":sQuery(id+"F5.wireOp",EDGE,"E9")}),1.0]])]});
            var Q1;
            Q1=makeQuery(id+"F5.imprint","IMPRINT",FACE,{"disambiguationData":[TD([[makeQuery(id+"F5.imprint","IMPRINT",EDGE,{"derivedFrom":sQuery(id+"F5.wireOp",EDGE,"E10")}),1.0]])]});
            extrude(context, id + "F11", {"entities" : qUnion([Q0, Q1]), "operationType" : NewBodyOperationType.REMOVE, "oppositeDirection" : true, "depth" : 3 * mm});
        }
    });
